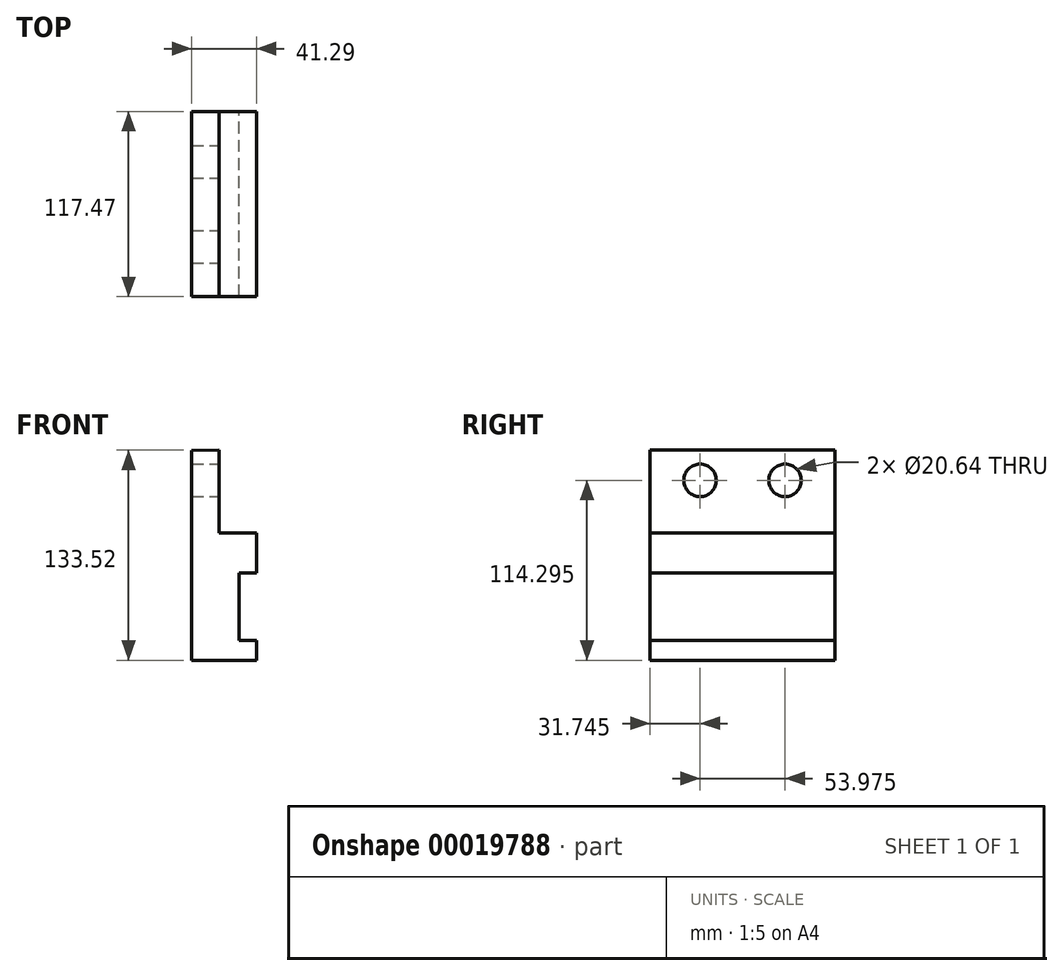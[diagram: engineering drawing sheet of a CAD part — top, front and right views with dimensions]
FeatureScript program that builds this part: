
annotation { "Feature Type Name" : "Feature", "Feature Type Description" : "" }
export const myFeature = defineFeature(function(context is Context, id is Id, definition is map)
    precondition{}
    {
        {
            var Q0;
            Q0=qCreatedBy(makeId("Front.planeOp"),FACE);
            var sketch = newSketch(context, id + "F0", { "sketchPlane" : qUnion([Q0])});
            skLineSegment(sketch, "E0", {"start": v(0, 0) * mm, "end": v(0, 66.67) * mm});
            skLineSegment(sketch, "E1", {"start": v(0, 0) * mm, "end": v(0, -66.67) * mm});
            skLineSegment(sketch, "E2", {"start": v(0, -66.67) * mm, "end": v(41.28, -66.67) * mm});
            skLineSegment(sketch, "E3", {"start": v(41.28, -66.68) * mm, "end": v(41.28, -53.98) * mm});
            skLineSegment(sketch, "E4", {"start": v(41.28, -53.98) * mm, "end": v(30.16, -53.98) * mm});
            skLineSegment(sketch, "E5", {"start": v(30.16, -53.98) * mm, "end": v(30.16, -11.11) * mm});
            skLineSegment(sketch, "E6", {"start": v(30.16, -11.11) * mm, "end": v(41.29, -11.11) * mm});
            skLineSegment(sketch, "E7", {"start": v(41.29, -11.11) * mm, "end": v(41.29, 14.29) * mm});
            skLineSegment(sketch, "E8", {"start": v(41.29, 14.29) * mm, "end": v(17.48, 14.29) * mm});
            skLineSegment(sketch, "E9", {"start": v(17.48, 14.29) * mm, "end": v(17.48, 66.85) * mm});
            skLineSegment(sketch, "E10", {"start": v(17.48, 66.85) * mm, "end": v(0, 66.67) * mm});
            skSolve(sketch);
        }
        {
            var Q0;
            Q0=makeQuery(id+"F0.imprint","IMPRINT",FACE,{"disambiguationData":[TD([[makeQuery(id+"F0.imprint","IMPRINT",EDGE,{"derivedFrom":sQuery(id+"F0.wireOp",EDGE,"E0")}),-1.0]])]});
            extrude(context, id + "F1", {"entities" : qUnion([Q0]), "depth" : 117.47 * mm});
        }
        {
            var Q0;
            Q0=makeQuery(id+"F1.opExtrude","SWEPT_FACE",FACE,{"disambiguationData":[OSD([sQuery(id+"F0.wireOp",EDGE,"E9")])]});
            var sketch = newSketch(context, id + "F2", { "sketchPlane" : qUnion([Q0])});
            skLineSegment(sketch, "E11", {"start": v(-117.48, 14.29) * mm, "end": v(-85.73, 14.29) * mm});
            skLineSegment(sketch, "E12", {"start": v(-85.73, 14.29) * mm, "end": v(-85.73, 47.62) * mm});
            skCircle(sketch, "E13", {"center": v(-85.73, 47.62) * mm, "radius": 10.32 * mm});
            skLineSegment(sketch, "E14", {"start": v(-85.73, 47.62) * mm, "end": v(-31.75, 47.62) * mm});
            skCircle(sketch, "E15", {"center": v(-31.75, 47.62) * mm, "radius": 10.32 * mm});
            skLineSegment(sketch, "E16", {"start": v(-31.75, 47.62) * mm, "end": v(-31.75, 14.29) * mm});
            skSolve(sketch);
        }
        {
            var Q0;
            Q0=sQuery(id+"F2.wireOp",VERTEX,"E12.end");
            var Q1;
            Q1=makeQuery(id+"F1.opExtrude","SWEPT_BODY",BODY,{"disambiguationData":[OSD([sQuery(id+"F0.wireOp",EDGE,"E0"),sQuery(id+"F0.wireOp",EDGE,"E1"),sQuery(id+"F0.wireOp",EDGE,"E2"),sQuery(id+"F0.wireOp",EDGE,"E3"),sQuery(id+"F0.wireOp",EDGE,"E4"),sQuery(id+"F0.wireOp",EDGE,"E5"),sQuery(id+"F0.wireOp",EDGE,"E6"),sQuery(id+"F0.wireOp",EDGE,"E7"),sQuery(id+"F0.wireOp",EDGE,"E8"),sQuery(id+"F0.wireOp",EDGE,"E9"),sQuery(id+"F0.wireOp",EDGE,"E10")])]});
            hole(context, id + "F3", {"style" : HoleStyle.SIMPLE, "holeDiameter" : 20.64 * mm, "endStyle" : HoleEndStyle.THROUGH, "locations" : qUnion([Q0]), "scope" : qUnion([Q1])});
        }
        {
            var Q0;
            Q0=sQuery(id+"F2.wireOp",VERTEX,"E15.center");
            var Q1;
            Q1=makeQuery(id+"F1.opExtrude","SWEPT_BODY",BODY,{"disambiguationData":[OSD([sQuery(id+"F0.wireOp",EDGE,"E0"),sQuery(id+"F0.wireOp",EDGE,"E1"),sQuery(id+"F0.wireOp",EDGE,"E2"),sQuery(id+"F0.wireOp",EDGE,"E3"),sQuery(id+"F0.wireOp",EDGE,"E4"),sQuery(id+"F0.wireOp",EDGE,"E5"),sQuery(id+"F0.wireOp",EDGE,"E6"),sQuery(id+"F0.wireOp",EDGE,"E7"),sQuery(id+"F0.wireOp",EDGE,"E8"),sQuery(id+"F0.wireOp",EDGE,"E9"),sQuery(id+"F0.wireOp",EDGE,"E10")])]});
            hole(context, id + "F4", {"style" : HoleStyle.SIMPLE, "holeDiameter" : 20.64 * mm, "endStyle" : HoleEndStyle.THROUGH, "locations" : qUnion([Q0]), "scope" : qUnion([Q1])});
        }
    });
